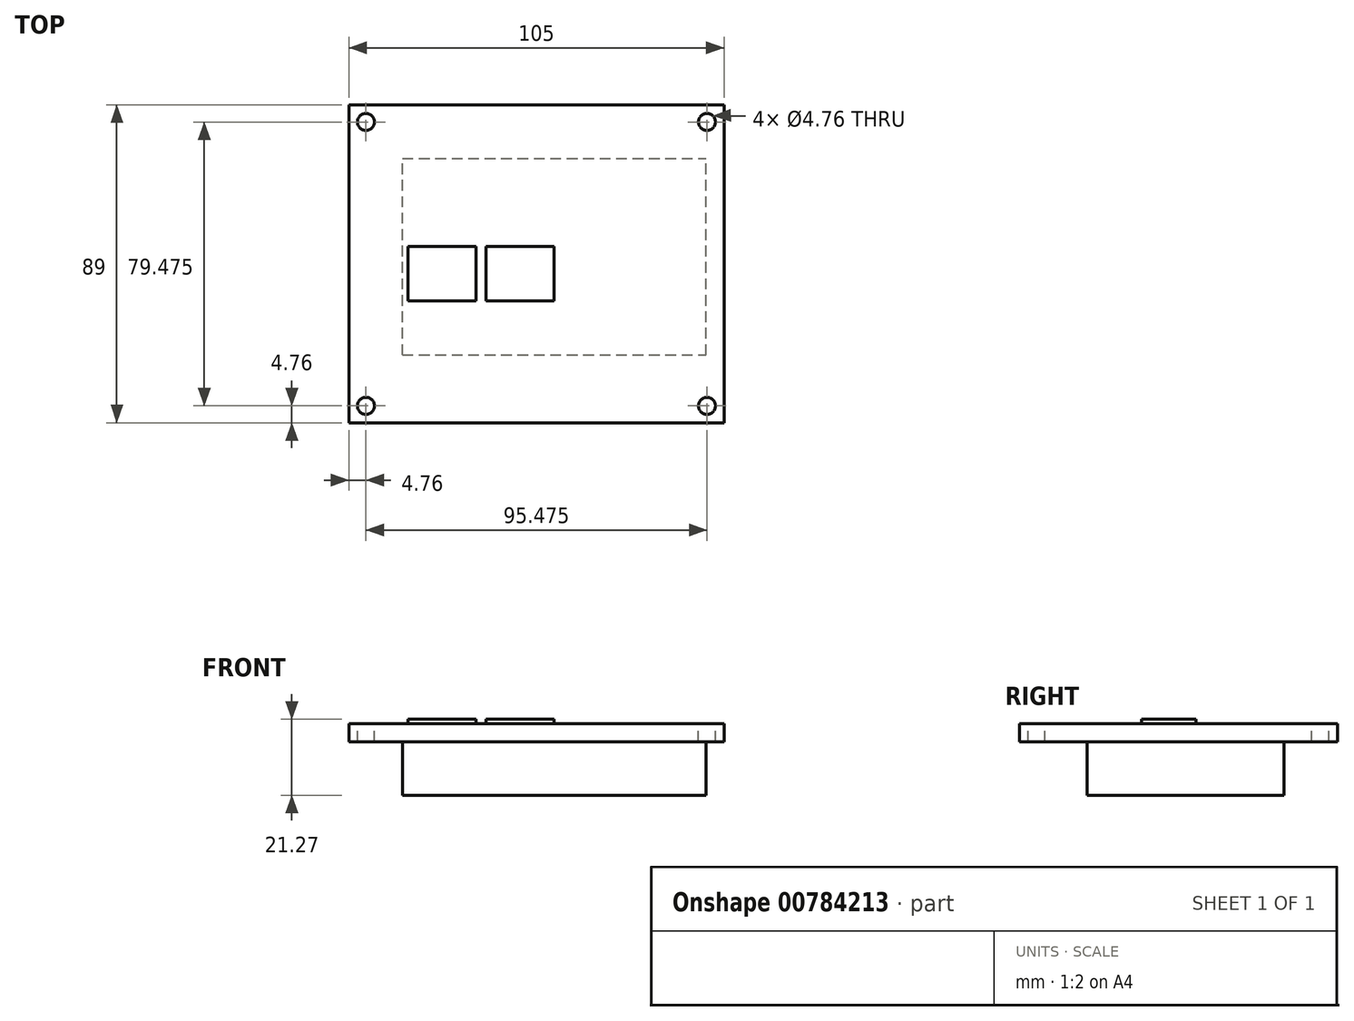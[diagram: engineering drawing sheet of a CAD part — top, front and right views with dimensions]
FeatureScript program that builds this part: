
annotation { "Feature Type Name" : "Feature", "Feature Type Description" : "" }
export const myFeature = defineFeature(function(context is Context, id is Id, definition is map)
    precondition{}
    {
        {
            var Q0;
            Q0=qCreatedBy(makeId("Top.planeOp"),FACE);
            var sketch = newSketch(context, id + "F0", { "sketchPlane" : qUnion([Q0])});
            skLineSegment(sketch, "E0.bottom", {"start": v(-60.65, 54.8) * mm, "end": v(44.35, 54.8) * mm});
            skLineSegment(sketch, "E0.top", {"start": v(-60.65, -34.2) * mm, "end": v(44.35, -34.2) * mm});
            skLineSegment(sketch, "E0.left", {"start": v(-60.65, 54.8) * mm, "end": v(-60.65, -34.2) * mm});
            skLineSegment(sketch, "E0.right", {"start": v(44.35, 54.8) * mm, "end": v(44.35, -34.2) * mm});
            skSolve(sketch);
        }
        {
            var Q0;
            Q0=makeQuery(id+"F0.imprint","IMPRINT",FACE,{"disambiguationData":[TD([[makeQuery(id+"F0.imprint","IMPRINT",EDGE,{"derivedFrom":sQuery(id+"F0.wireOp",EDGE,"E0.bottom")}),-1.0]])]});
            var sketch = newSketch(context, id + "F1", { "sketchPlane" : qUnion([Q0])});
            skLineSegment(sketch, "E1.bottom", {"start": v(-45.65, -15.2) * mm, "end": v(39.35, -15.2) * mm});
            skLineSegment(sketch, "E1.top", {"start": v(-45.65, 39.8) * mm, "end": v(39.35, 39.8) * mm});
            skLineSegment(sketch, "E1.left", {"start": v(-45.65, -15.2) * mm, "end": v(-45.65, 39.8) * mm});
            skLineSegment(sketch, "E1.right", {"start": v(39.35, -15.2) * mm, "end": v(39.35, 39.8) * mm});
            skSolve(sketch);
        }
        {
            var Q0;
            Q0=makeQuery(id+"F0.imprint","IMPRINT",FACE,{"disambiguationData":[TD([[makeQuery(id+"F0.imprint","IMPRINT",EDGE,{"derivedFrom":sQuery(id+"F0.wireOp",EDGE,"E0.bottom")}),-1.0]])]});
            extrude(context, id + "F2", {"entities" : qUnion([Q0]), "depth" : 5 * mm, "offsetDistance" : 25.4 * mm});
        }
        {
            var Q0;
            Q0=makeQuery(id+"F1.imprint","IMPRINT",FACE,{"disambiguationData":[TD([[makeQuery(id+"F1.imprint","IMPRINT",EDGE,{"derivedFrom":sQuery(id+"F1.wireOp",EDGE,"E1.bottom")}),1.0]])]});
            extrude(context, id + "F3", {"entities" : qUnion([Q0]), "operationType" : NewBodyOperationType.ADD, "oppositeDirection" : true, "depth" : 15 * mm, "offsetDistance" : 25.4 * mm});
        }
        {
            var Q0;
            Q0=makeQuery(id+"F2.opExtrude","CAP_FACE",FACE,{"disambiguationData":[OSD([sQuery(id+"F0.wireOp",EDGE,"E0.bottom"),sQuery(id+"F0.wireOp",EDGE,"E0.top"),sQuery(id+"F0.wireOp",EDGE,"E0.left"),sQuery(id+"F0.wireOp",EDGE,"E0.right")])],"isStart":false});
            var sketch = newSketch(context, id + "F4", { "sketchPlane" : qUnion([Q0])});
            skLineSegment(sketch, "E2.bottom", {"start": v(-44.11, 15.24) * mm, "end": v(-25.06, 15.24) * mm});
            skLineSegment(sketch, "E2.top", {"start": v(-44.11, 0) * mm, "end": v(-25.06, 0) * mm});
            skLineSegment(sketch, "E2.left", {"start": v(-44.11, 15.24) * mm, "end": v(-44.11, 0) * mm});
            skLineSegment(sketch, "E2.right", {"start": v(-25.06, 15.24) * mm, "end": v(-25.06, 0) * mm});
            skLineSegment(sketch, "E3.bottom", {"start": v(-22.29, 15.24) * mm, "end": v(-3.24, 15.24) * mm});
            skLineSegment(sketch, "E3.top", {"start": v(-22.29, 0) * mm, "end": v(-3.24, 0) * mm});
            skLineSegment(sketch, "E3.left", {"start": v(-22.29, 15.24) * mm, "end": v(-22.29, 0) * mm});
            skLineSegment(sketch, "E3.right", {"start": v(-3.24, 15.24) * mm, "end": v(-3.24, 0) * mm});
            skSolve(sketch);
        }
        {
            var Q0;
            Q0=makeQuery(id+"F4.imprint","IMPRINT",FACE,{"disambiguationData":[TD([[makeQuery(id+"F4.imprint","IMPRINT",EDGE,{"derivedFrom":sQuery(id+"F4.wireOp",EDGE,"E2.bottom")}),-1.0]])]});
            var Q1;
            Q1=makeQuery(id+"F4.imprint","IMPRINT",FACE,{"disambiguationData":[TD([[makeQuery(id+"F4.imprint","IMPRINT",EDGE,{"derivedFrom":sQuery(id+"F4.wireOp",EDGE,"E3.bottom")}),-1.0]])]});
            extrude(context, id + "F5", {"entities" : qUnion([Q0, Q1]), "operationType" : NewBodyOperationType.ADD, "depth" : 1.27 * mm, "offsetDistance" : 25.4 * mm});
        }
        {
            var Q0;
            Q0=makeQuery(id+"F2.opExtrude","CAP_FACE",FACE,{"disambiguationData":[OSD([sQuery(id+"F0.wireOp",EDGE,"E0.bottom"),sQuery(id+"F0.wireOp",EDGE,"E0.top"),sQuery(id+"F0.wireOp",EDGE,"E0.left"),sQuery(id+"F0.wireOp",EDGE,"E0.right")])],"isStart":false});
            var sketch = newSketch(context, id + "F6", { "sketchPlane" : qUnion([Q0])});
            skPoint(sketch, "E4", {"position": v(-55.9, 50.04) * mm});
            skPoint(sketch, "E5", {"position": v(-55.9, -29.44) * mm});
            skPoint(sketch, "E6", {"position": v(39.58, -29.44) * mm});
            skPoint(sketch, "E7", {"position": v(39.58, 50.04) * mm});
            skLineSegment(sketch, "E8", {"start": v(-55.9, 50.04) * mm, "end": v(39.58, 50.04) * mm});
            skLineSegment(sketch, "E9", {"start": v(39.58, -29.44) * mm, "end": v(39.58, 50.04) * mm});
            skLineSegment(sketch, "E10", {"start": v(39.58, -29.44) * mm, "end": v(-55.9, -29.44) * mm});
            skLineSegment(sketch, "E11", {"start": v(-55.9, -29.44) * mm, "end": v(-55.9, 50.04) * mm});
            skLineSegment(sketch, "E12.bottom", {"start": v(-55.9, 43.69) * mm, "end": v(42.53, 43.69) * mm});
            skLineSegment(sketch, "E12.top", {"start": v(-55.9, -24.58) * mm, "end": v(42.53, -24.58) * mm});
            skLineSegment(sketch, "E12.left", {"start": v(-55.9, 43.69) * mm, "end": v(-55.9, -24.58) * mm});
            skLineSegment(sketch, "E12.right", {"start": v(42.53, 43.69) * mm, "end": v(42.53, -24.58) * mm});
            skSolve(sketch);
        }
        {
            var Q0;
            Q0=sQuery(id+"F6.wireOp",VERTEX,"E4");
            var Q1;
            Q1=sQuery(id+"F6.wireOp",VERTEX,"E5");
            var Q2;
            Q2=sQuery(id+"F6.wireOp",VERTEX,"E7");
            var Q3;
            Q3=sQuery(id+"F6.wireOp",VERTEX,"E6");
            var Q4;
            Q4=makeQuery(id+"F2.opExtrude","SWEPT_BODY",BODY,{"disambiguationData":[OSD([sQuery(id+"F0.wireOp",EDGE,"E0.bottom"),sQuery(id+"F0.wireOp",EDGE,"E0.top"),sQuery(id+"F0.wireOp",EDGE,"E0.left"),sQuery(id+"F0.wireOp",EDGE,"E0.right")])]});
            hole(context, id + "F7", {"style" : HoleStyle.SIMPLE, "endStyle" : HoleEndStyle.THROUGH, "holeDiameter" : 4.76 * mm, "majorDiameter" : 6.35 * mm, "isTappedThrough" : true, "tappedDepth" : 12.7 * mm, "tapClearance" : 3, "locations" : qUnion([Q0, Q1, Q2, Q3]), "scope" : qUnion([Q4])});
        }
    });
